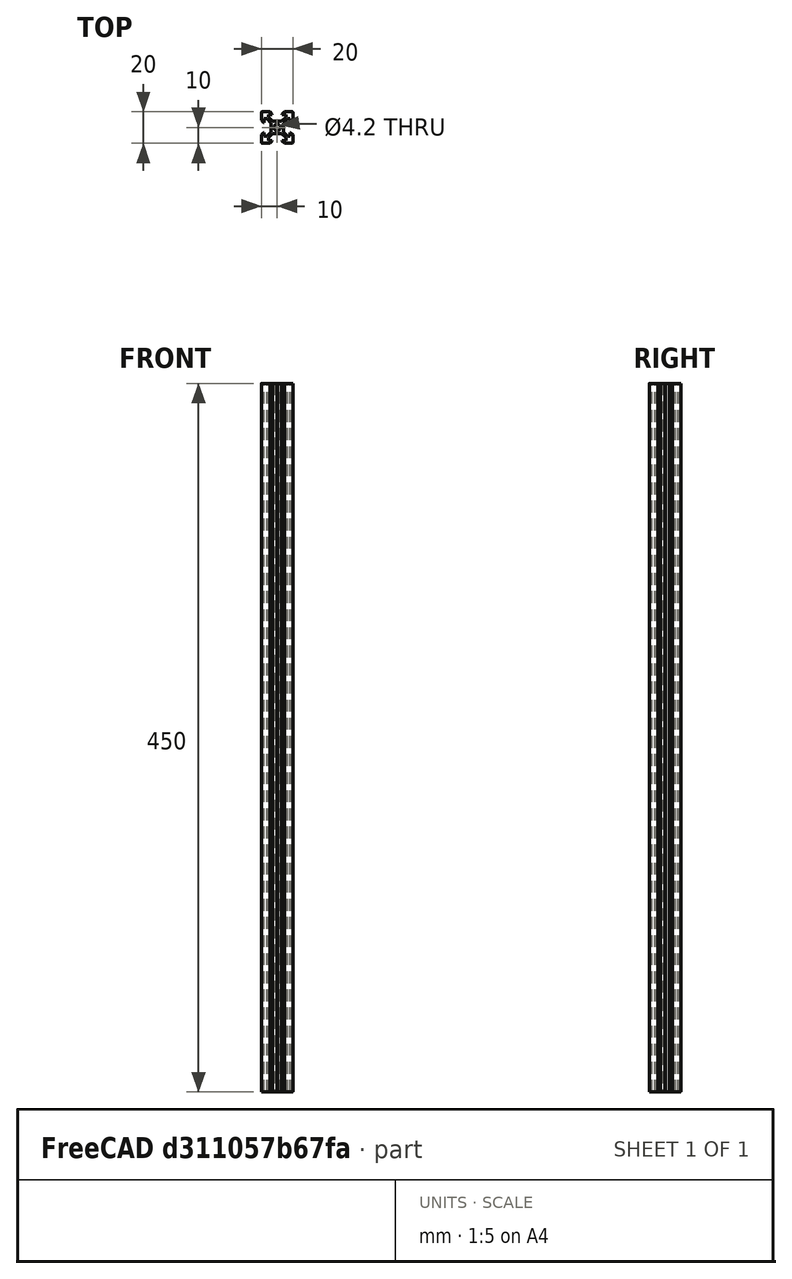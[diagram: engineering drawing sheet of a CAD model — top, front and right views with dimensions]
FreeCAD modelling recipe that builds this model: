
FCSTD DOCUMENT  (FreeCAD 0.20R25566 (Git))
Label: 2020-450
License: All rights reserved
LicenseURL: http://en.wikipedia.org/wiki/All_rights_reserved
objects: Sketcher::SketchObject×1, PartDesign::Pad×1, PartDesign::Body×1
note: 4 computed .brp shape members not serialized (recipe doc carries the construction recipe); baked Part::Feature solids carry a one-line shape summary decoded from their .brp

FEATURE [Sketcher::SketchObject] Sketch
  FullyConstrained = true
  MapMode = 5
  Support = -> [XY_Plane]
  sketch-geometry (65):
    g0: LineSegment StartX=-10 StartY=4.58 StartZ=0 EndX=-10 EndY=9.5 EndZ=0
    g1: LineSegment StartX=-9.5 StartY=10 StartZ=0 EndX=-4.58 EndY=10 EndZ=0
    g2: LineSegment StartX=-5.5 StartY=8.2 StartZ=0 EndX=-3.125 EndY=8.2 EndZ=0
    g3: LineSegment StartX=-8.2 StartY=5.5 StartZ=0 EndX=-8.2 EndY=3.125 EndZ=0
    g4: LineSegment StartX=-0.125 StartY=3.9 StartZ=0 EndX=-2.83934 EndY=3.9 EndZ=0
    g5: LineSegment StartX=-3.9 StartY=2.83934 StartZ=0 EndX=-3.9 EndY=0.125 EndZ=0
    g6: ArcOfCircle CenterX=0 CenterY=3.9 CenterZ=0 NormalX=0 NormalY=0 NormalZ=1 AngleXU=0 Radius=0.125 StartAngle=3.14159 EndAngle=6.28319
    g7: ArcOfCircle CenterX=-3.9 CenterY=0 CenterZ=0 NormalX=0 NormalY=0 NormalZ=1 AngleXU=0 Radius=0.125 StartAngle=4.71239 EndAngle=7.85398
    g8: ArcOfCircle CenterX=-9.5 CenterY=9.5 CenterZ=0 NormalX=0 NormalY=0 NormalZ=1 AngleXU=0 Radius=0.5 StartAngle=1.5708 EndAngle=3.14159
    g9: LineSegment StartX=-5.5 StartY=8.2 StartZ=0 EndX=-5.5 EndY=6.56066 EndZ=0
    g10: LineSegment StartX=-8.2 StartY=5.5 StartZ=0 EndX=-6.56066 EndY=5.5 EndZ=0
    g11: LineSegment StartX=-4.58 StartY=10 StartZ=0 EndX=-3.125 EndY=8.545 EndZ=0
    g12: LineSegment StartX=-3.125 StartY=8.545 StartZ=0 EndX=-3.125 EndY=8.2 EndZ=0
    g13: LineSegment StartX=-10 StartY=4.58 StartZ=0 EndX=-8.545 EndY=3.125 EndZ=0
    g14: LineSegment StartX=-8.545 StartY=3.125 StartZ=0 EndX=-8.2 EndY=3.125 EndZ=0
    g15: LineSegment StartX=-5.5 StartY=6.56066 StartZ=0 EndX=-2.83934 EndY=3.9 EndZ=0
    g16: LineSegment StartX=-6.56066 StartY=5.5 StartZ=0 EndX=-3.9 EndY=2.83934 EndZ=0
    g17: Circle CenterX=0 CenterY=0 CenterZ=0 NormalX=0 NormalY=0 NormalZ=1 AngleXU=0 Radius=2.1
    g18: LineSegment StartX=0.125 StartY=3.9 StartZ=0 EndX=2.83934 EndY=3.9 EndZ=0
    g19: LineSegment StartX=2.83934 StartY=3.9 StartZ=0 EndX=5.5 EndY=6.56066 EndZ=0
    g20: LineSegment StartX=5.5 StartY=6.56066 StartZ=0 EndX=5.5 EndY=8.2 EndZ=0
    g21: LineSegment StartX=3.125 StartY=8.2 StartZ=0 EndX=3.125 EndY=8.545 EndZ=0
    g22: LineSegment StartX=5.5 StartY=8.2 StartZ=0 EndX=3.125 EndY=8.2 EndZ=0
    g23: LineSegment StartX=4.58 StartY=10 StartZ=0 EndX=9.5 EndY=10 EndZ=0
    g24: ArcOfCircle CenterX=9.5 CenterY=9.5 CenterZ=0 NormalX=0 NormalY=0 NormalZ=1 AngleXU=0 Radius=0.5 StartAngle=1.9e-15 EndAngle=1.5708
    g25: LineSegment StartX=10 StartY=9.5 StartZ=0 EndX=10 EndY=4.58 EndZ=0
    g26: LineSegment StartX=10 StartY=4.58 StartZ=0 EndX=8.545 EndY=3.125 EndZ=0
    g27: LineSegment StartX=8.545 StartY=3.125 StartZ=0 EndX=8.2 EndY=3.125 EndZ=0
    g28: LineSegment StartX=8.2 StartY=3.125 StartZ=0 EndX=8.2 EndY=5.5 EndZ=0
    g29: LineSegment StartX=8.2 StartY=5.5 StartZ=0 EndX=6.56066 EndY=5.5 EndZ=0
    g30: LineSegment StartX=6.56066 StartY=5.5 StartZ=0 EndX=3.9 EndY=2.83934 EndZ=0
    g31: LineSegment StartX=3.9 StartY=2.83934 StartZ=0 EndX=3.9 EndY=0.125 EndZ=0
    g32: ArcOfCircle CenterX=3.9 CenterY=0 CenterZ=0 NormalX=0 NormalY=0 NormalZ=1 AngleXU=0 Radius=0.125 StartAngle=1.5708 EndAngle=4.71239
    g33: LineSegment StartX=3.9 StartY=-0.125 StartZ=0 EndX=3.9 EndY=-2.83934 EndZ=0
    g34: LineSegment StartX=3.9 StartY=-2.83934 StartZ=0 EndX=6.56066 EndY=-5.5 EndZ=0
    g35: LineSegment StartX=6.56066 StartY=-5.5 StartZ=0 EndX=8.2 EndY=-5.5 EndZ=0
    g36: LineSegment StartX=8.2 StartY=-5.5 StartZ=0 EndX=8.2 EndY=-3.125 EndZ=0
    g37: LineSegment StartX=8.2 StartY=-3.125 StartZ=0 EndX=8.545 EndY=-3.125 EndZ=0
    g38: LineSegment StartX=8.545 StartY=-3.125 StartZ=0 EndX=10 EndY=-4.58 EndZ=0
    g39: LineSegment StartX=10 StartY=-4.58 StartZ=0 EndX=10 EndY=-9.5 EndZ=0
    g40: ArcOfCircle CenterX=9.5 CenterY=-9.5 CenterZ=0 NormalX=0 NormalY=0 NormalZ=1 AngleXU=0 Radius=0.5 StartAngle=4.71239 EndAngle=6.28319
    g41: LineSegment StartX=9.5 StartY=-10 StartZ=0 EndX=4.58 EndY=-10 EndZ=0
    g42: LineSegment StartX=4.58 StartY=-10 StartZ=0 EndX=3.125 EndY=-8.545 EndZ=0
    g43: LineSegment StartX=2.83934 StartY=-3.9 StartZ=0 EndX=5.5 EndY=-6.56066 EndZ=0
    g44: LineSegment StartX=3.125 StartY=-8.545 StartZ=0 EndX=3.125 EndY=-8.2 EndZ=0
    g45: LineSegment StartX=3.125 StartY=-8.2 StartZ=0 EndX=5.5 EndY=-8.2 EndZ=0
    g46: LineSegment StartX=5.5 StartY=-8.2 StartZ=0 EndX=5.5 EndY=-6.56066 EndZ=0
    g47: ArcOfCircle CenterX=0 CenterY=-3.9 CenterZ=0 NormalX=0 NormalY=0 NormalZ=1 AngleXU=0 Radius=0.125 StartAngle=0 EndAngle=3.14159
    g48: LineSegment StartX=0.125 StartY=-3.9 StartZ=0 EndX=2.83934 EndY=-3.9 EndZ=0
    g49: LineSegment StartX=-0.125 StartY=-3.9 StartZ=0 EndX=-2.83934 EndY=-3.9 EndZ=0
    g50: LineSegment StartX=-3.9 StartY=-0.125 StartZ=0 EndX=-3.9 EndY=-2.83934 EndZ=0
    g51: LineSegment StartX=-3.9 StartY=-2.83934 StartZ=0 EndX=-6.56066 EndY=-5.5 EndZ=0
    g52: LineSegment StartX=-6.56066 StartY=-5.5 StartZ=0 EndX=-8.2 EndY=-5.5 EndZ=0
    g53: LineSegment StartX=-8.2 StartY=-5.5 StartZ=0 EndX=-8.2 EndY=-3.125 EndZ=0
    g54: LineSegment StartX=-8.2 StartY=-3.125 StartZ=0 EndX=-8.545 EndY=-3.125 EndZ=0
    g55: LineSegment StartX=-8.545 StartY=-3.125 StartZ=0 EndX=-10 EndY=-4.58 EndZ=0
    g56: LineSegment StartX=-10 StartY=-4.58 StartZ=0 EndX=-10 EndY=-9.5 EndZ=0
    g57: ArcOfCircle CenterX=-9.5 CenterY=-9.5 CenterZ=0 NormalX=0 NormalY=0 NormalZ=1 AngleXU=0 Radius=0.5 StartAngle=3.14159 EndAngle=4.71239
    g58: LineSegment StartX=-9.5 StartY=-10 StartZ=0 EndX=-4.58 EndY=-10 EndZ=0
    g59: LineSegment StartX=-4.58 StartY=-10 StartZ=0 EndX=-3.125 EndY=-8.545 EndZ=0
    g60: LineSegment StartX=-2.83934 StartY=-3.9 StartZ=0 EndX=-5.5 EndY=-6.56066 EndZ=0
    g61: LineSegment StartX=-5.5 StartY=-6.56066 StartZ=0 EndX=-5.5 EndY=-8.2 EndZ=0
    g62: LineSegment StartX=-5.5 StartY=-8.2 StartZ=0 EndX=-3.125 EndY=-8.2 EndZ=0
    g63: LineSegment StartX=-3.125 StartY=-8.545 StartZ=0 EndX=-3.125 EndY=-8.2 EndZ=0
    g64: LineSegment StartX=3.125 StartY=8.545 StartZ=0 EndX=4.58 EndY=10 EndZ=0
  constraints (194):
    c: Diameter(g17) = 4.2
    c: Radius(g32) = 0.125
    c: Coincident(g-1,g17)
    c: DistanceY(g57,g1) = 20
    c: DistanceX(g56,g39) = 20
    c: Radius(g57) = 0.5
    c: DistanceX(g56,g17) = 10
    c: DistanceY(g57,g17) = 10
    c: Distance(g5,g4) = 1.5
    c: DistanceY(g20,g23) = 1.8
    c: DistanceY(g18,g20) = 4.3
    c: DistanceX(g11,g21) = 6.25
    c: DistanceX(g1,g23) = 9.16
    c: DistanceX(g2,g20) = 11
    c: Coincident(g6,g18)
    c: Coincident(g6,g4)
    c: Coincident(g4,g15)
    c: Coincident(g18,g19)
    c: Coincident(g5,g16)
    c: Coincident(g16,g10)
    c: Coincident(g15,g9)
    c: Coincident(g12,g2)
    c: Coincident(g2,g9)
    c: Coincident(g12,g11)
    c: Coincident(g1,g11)
    c: Coincident(g23,g64)
    c: Coincident(g22,g21)
    c: Coincident(g64,g21)
    c: Coincident(g22,g20)
    c: Coincident(g19,g20)
    c: Coincident(g25,g26)
    c: Coincident(g27,g26)
    c: Coincident(g27,g28)
    c: Coincident(g28,g29)
    c: Coincident(g29,g30)
    c: Coincident(g0,g13)
    c: Coincident(g14,g13)
    c: Coincident(g14,g3)
    c: Coincident(g3,g10)
    c: Coincident(g5,g7)
    c: Coincident(g50,g7)
    c: Coincident(g51,g50)
    c: Coincident(g52,g51)
    c: Coincident(g52,g53)
    c: Coincident(g54,g53)
    c: Coincident(g55,g54)
    c: Coincident(g56,g55)
    c: Coincident(g58,g59)
    c: Coincident(g63,g59)
    c: Coincident(g62,g63)
    c: Coincident(g62,g61)
    c: Coincident(g60,g61)
    c: Coincident(g49,g60)
    c: Coincident(g47,g49)
    c: Coincident(g48,g47)
    c: Coincident(g48,g43)
    c: Coincident(g46,g43)
    c: Coincident(g45,g46)
    c: Coincident(g45,g44)
    c: Coincident(g42,g44)
    c: Coincident(g41,g42)
    c: Coincident(g39,g38)
    c: Coincident(g38,g37)
    c: Coincident(g37,g36)
    c: Coincident(g35,g36)
    c: Coincident(g34,g35)
    c: Coincident(g34,g33)
    c: Coincident(g31,g30)
    c: Coincident(g33,g32)
    c: Coincident(g32,g31)
    c: Vertical(g0)
    c: Horizontal(g1)
    c: Equal(g0,g1)
    c: Horizontal(g4)
    c: PointOnObject(g6,g-2)
    c: Horizontal(g18)
    c: Horizontal(g4,g6)
    c: Horizontal(g6,g6)
    c: Parallel(g13,g11)
    c: Horizontal(g14)
    c: Vertical(g12)
    c: Equal(g14,g12)
    c: Vertical(g3)
    c: Horizontal(g2)
    c: Equal(g3,g2)
    c: Equal(g10,g9)
    c: Horizontal(g10)
    c: Vertical(g9)
    c: Parallel(g16,g15)
    c: Equal(g13,g11)
    c: Tangent(g8,g0) = 1.5708
    c: PointOnObject(g7,g-1)
    c: Vertical(g5)
    c: Vertical(g50)
    c: Vertical(g7,g7)
    c: Vertical(g7,g5)
    c: Horizontal(g52)
    c: Vertical(g53)
    c: Horizontal(g54)
    c: Vertical(g56)
    c: Equal(g50,g5)
    c: Equal(g51,g16)
    c: Perpendicular(g16,g51)
    c: Equal(g52,g10)
    c: Equal(g53,g3)
    c: Equal(g54,g14)
    c: Equal(g55,g13)
    c: Perpendicular(g55,g13)
    c: Equal(g56,g0)
    c: Tangent(g57,g56) = -1.5708
    c: Tangent(g57,g58) = -1.5708
    c: Tangent(g8,g1) = 1.5708
    c: Equal(g57,g8)
    c: Horizontal(g58)
    c: Equal(g58,g56)
    c: Equal(g55,g59)
    c: Parallel(g55,g59)
    c: Vertical(g63)
    c: Equal(g63,g54)
    c: Horizontal(g62)
    c: Vertical(g61)
    c: Equal(g61,g52)
    c: Equal(g60,g51)
    c: Parallel(g60,g51)
    c: PointOnObject(g47,g-2)
    c: Horizontal(g47,g47)
    c: Horizontal(g47,g47)
    c: Horizontal(g49)
    c: Equal(g49,g50)
    c: Horizontal(g48)
    c: Vertical(g46)
    c: Perpendicular(g60,g43)
    c: Equal(g43,g60)
    c: Equal(g46,g61)
    c: Horizontal(g45)
    c: Equal(g45,g62)
    c: Vertical(g44)
    c: Equal(g44,g63)
    c: Perpendicular(g42,g59)
    c: Equal(g42,g59)
    c: Horizontal(g41)
    c: Equal(g58,g41)
    c: Tangent(g40,g41) = 1.5708
    c: Tangent(g40,g39) = 1.5708
    c: Equal(g57,g40)
    c: Vertical(g39)
    c: Equal(g41,g39)
    c: Parallel(g42,g38)
    c: Equal(g42,g38)
    c: Horizontal(g37)
    c: Equal(g44,g37)
    c: Vertical(g36)
    c: Equal(g45,g36)
    c: Horizontal(g35)
    c: Equal(g35,g46)
    c: Parallel(g43,g34)
    c: Equal(g43,g34)
    c: PointOnObject(g32,g-1)
    c: Vertical(g33)
    c: Vertical(g32,g31)
    c: Vertical(g31,g32)
    c: Equal(g48,g33)
    c: Equal(g47,g7)
    c: Equal(g7,g6)
    c: Vertical(g31)
    c: Equal(g33,g31)
    c: Equal(g4,g5)
    c: Equal(g4,g18)
    c: Parallel(g30,g19)
    c: Equal(g30,g19)
    c: Horizontal(g29)
    c: Vertical(g20)
    c: Equal(g35,g29)
    c: Equal(g29,g20)
    c: Horizontal(g22)
    c: Equal(g22,g2)
    c: Vertical(g21)
    c: Equal(g11,g64)
    c: Horizontal(g23)
    c: Equal(g1,g23)
    c: Vertical(g28)
    c: Equal(g28,g36)
    c: Horizontal(g27)
    c: Equal(g27,g37)
    c: Perpendicular(g38,g26)
    c: Equal(g38,g26)
    c: Vertical(g25)
    c: Equal(g39,g25)
    c: Tangent(g24,g23) = 1.5708
    c: Tangent(g24,g25) = 1.5708
    c: Vertical(g25,g38)
    c: Horizontal(g2,g21)
    c: Vertical(g10,g51)
    c: Angle(g64,g11) = 1.5708
FEATURE [PartDesign::Pad] Pad
  Direction = (0,0,1)
  Length = 450
  Length2 = 100
  Profile = -> Sketch
  Type = 0
FEATURE [PartDesign::Body] Body  label="2020-400"
  Group = -> [Sketch,Pad]
  Origin = -> Origin
  Tip = -> Pad
